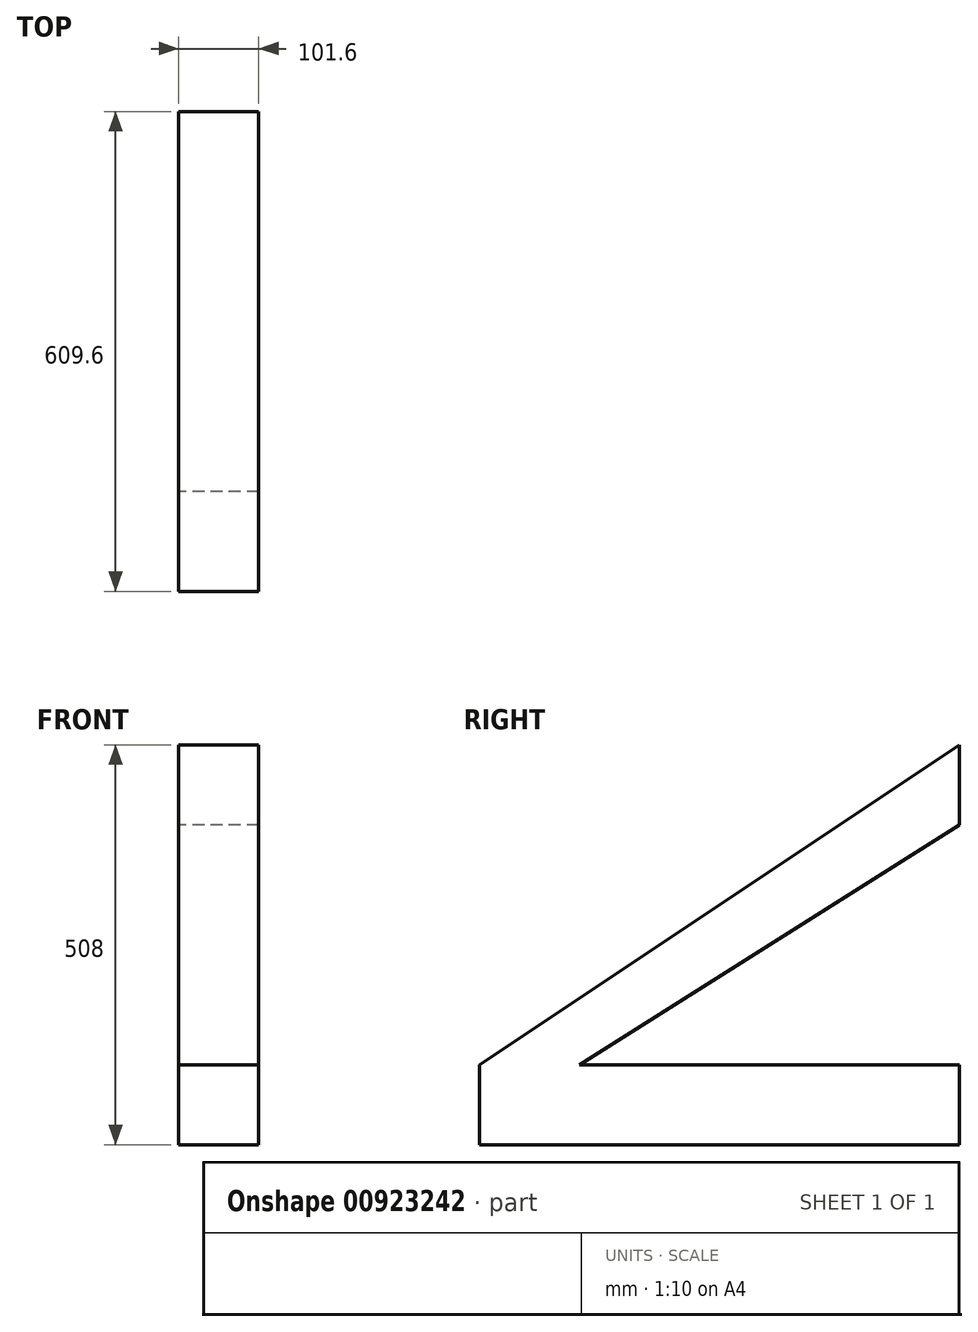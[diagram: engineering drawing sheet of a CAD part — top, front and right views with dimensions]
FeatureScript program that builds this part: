
annotation { "Feature Type Name" : "Feature", "Feature Type Description" : "" }
export const myFeature = defineFeature(function(context is Context, id is Id, definition is map)
    precondition{}
    {
        {
            var Q0;
            Q0=qCreatedBy(makeId("Right.planeOp"),FACE);
            var sketch = newSketch(context, id + "F0", { "sketchPlane" : qUnion([Q0])});
            skLineSegment(sketch, "E0.bottom", {"start": v(0, -560) * mm, "end": v(-609.6, -560) * mm});
            skLineSegment(sketch, "E0.top", {"start": v(0, -458.4) * mm, "end": v(-609.6, -458.4) * mm});
            skLineSegment(sketch, "E0.left", {"start": v(0, -560) * mm, "end": v(0, -458.4) * mm});
            skLineSegment(sketch, "E0.right", {"start": v(-609.6, -560) * mm, "end": v(-609.6, -458.4) * mm});
            skLineSegment(sketch, "E1", {"start": v(0, -458.4) * mm, "end": v(0, -52) * mm});
            skLineSegment(sketch, "E2", {"start": v(0, -52) * mm, "end": v(-609.6, -458.4) * mm});
            skLineSegment(sketch, "E3", {"start": v(-482.6, -458.4) * mm, "end": v(0, -153.6) * mm});
            skSolve(sketch);
        }
        {
            var Q0;
            {var subQ0=sQuery(id+"F0.wireOp",EDGE,"E2");Q0=makeQuery(id+"F0.imprint","IMPRINT",FACE,{"disambiguationData":[TD([[makeQuery(id+"F0.imprint","IMPRINT",EDGE,{"derivedFrom":subQ0}),1.0]])]});}
            var Q1;
            Q1=makeQuery(id+"F0.imprint","IMPRINT",FACE,{"disambiguationData":[TD([[makeQuery(id+"F0.imprint","IMPRINT",EDGE,{"derivedFrom":sQuery(id+"F0.wireOp",EDGE,"E0.bottom")}),-1.0]])]});
            extrude(context, id + "F1", {"entities" : qUnion([Q0, Q1]), "depth" : 101.6 * mm, "offsetDistance" : 25.4 * mm});
        }
    });
